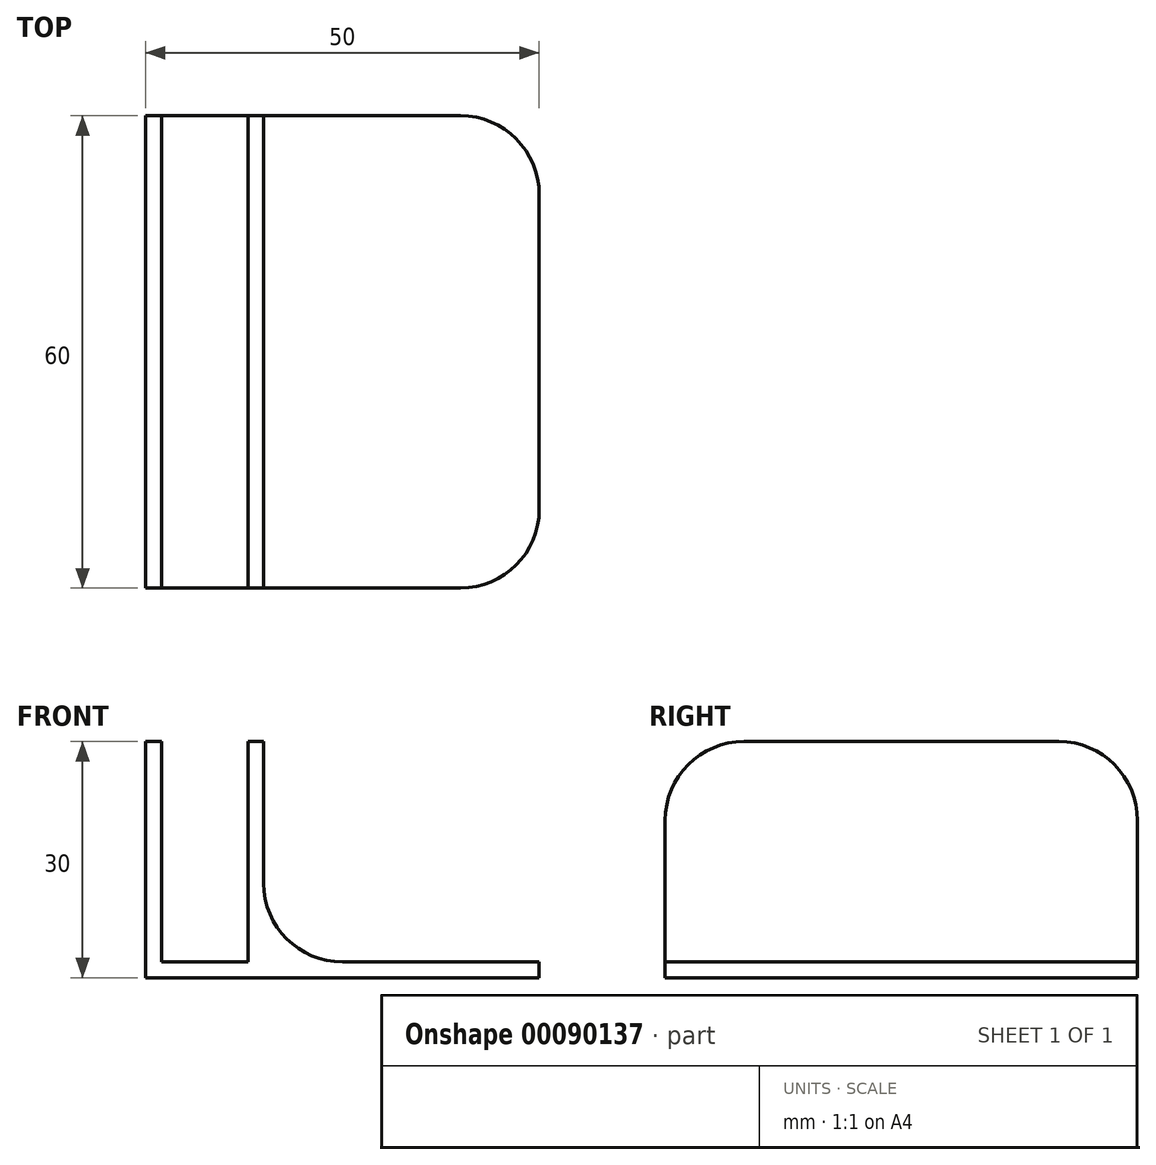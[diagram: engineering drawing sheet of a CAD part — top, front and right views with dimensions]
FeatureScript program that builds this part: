
annotation { "Feature Type Name" : "Feature", "Feature Type Description" : "" }
export const myFeature = defineFeature(function(context is Context, id is Id, definition is map)
    precondition{}
    {
        {
            var Q0;
            Q0=qCreatedBy(makeId("Front.planeOp"),FACE);
            var sketch = newSketch(context, id + "F0", { "sketchPlane" : qUnion([Q0])});
            skLineSegment(sketch, "E0.bottom", {"start": v(0, 0) * mm, "end": v(50, 0) * mm});
            skLineSegment(sketch, "E0.top", {"start": v(0, 2) * mm, "end": v(50, 2) * mm});
            skLineSegment(sketch, "E0.left", {"start": v(0, 0) * mm, "end": v(0, 2) * mm});
            skLineSegment(sketch, "E0.right", {"start": v(50, 0) * mm, "end": v(50, 2) * mm});
            skLineSegment(sketch, "E1.bottom", {"start": v(0, 0) * mm, "end": v(2, 0) * mm});
            skLineSegment(sketch, "E1.top", {"start": v(0, 30) * mm, "end": v(2, 30) * mm});
            skLineSegment(sketch, "E1.left", {"start": v(0, 0) * mm, "end": v(0, 30) * mm});
            skLineSegment(sketch, "E1.right", {"start": v(2, 0) * mm, "end": v(2, 30) * mm});
            skLineSegment(sketch, "E2.1.0.0", {"start": v(13, 0) * mm, "end": v(13, 30) * mm});
            skLineSegment(sketch, "E2.1.0.1", {"start": v(15, 0) * mm, "end": v(15, 30) * mm});
            skLineSegment(sketch, "E2.1.0.2", {"start": v(13, 0) * mm, "end": v(13, 2) * mm});
            skLineSegment(sketch, "E2.1.0.3", {"start": v(13, 0) * mm, "end": v(15, 0) * mm});
            skLineSegment(sketch, "E2.1.0.4", {"start": v(13, 30) * mm, "end": v(15, 30) * mm});
            skLineSegment(sketch, "E2.direction1", {"start": v(0, 0) * mm, "end": v(13, 0) * mm, "construction": true});
            skSolve(sketch);
        }
        {
            var Q0;
            Q0=qSketchRegion(id+"F0",true);
            extrude(context, id + "F1", {"entities" : qUnion([Q0]), "depth" : 60 * mm});
        }
        {
            var Q0;
            Q0=makeQuery(id+"F1.opExtrude","CAP_EDGE",EDGE,{"disambiguationData":[OSD([sQuery(id+"F0.wireOp",EDGE,"E2.1.0.4")])],"isStart":false});
            var Q1;
            Q1=makeQuery(id+"F1.opExtrude","CAP_EDGE",EDGE,{"disambiguationData":[OSD([sQuery(id+"F0.wireOp",EDGE,"E1.top")])],"isStart":false});
            var Q2;
            Q2=makeQuery(id+"F1.opExtrude","CAP_EDGE",EDGE,{"disambiguationData":[OSD([sQuery(id+"F0.wireOp",EDGE,"E2.1.0.4")])],"isStart":true});
            var Q3;
            Q3=makeQuery(id+"F1.opExtrude","CAP_EDGE",EDGE,{"disambiguationData":[OSD([sQuery(id+"F0.wireOp",EDGE,"E1.top")])],"isStart":true});
            var Q4;
            Q4=makeQuery(id+"F1.opExtrude","SWEPT_EDGE",EDGE,{"disambiguationData":[OSD([sQuery(id+"F0.wireOp",EDGE,"E0.top"),sQuery(id+"F0.wireOp",EDGE,"E2.1.0.1")])]});
            var Q5;
            Q5=makeQuery(id+"F1.opExtrude","CAP_EDGE",EDGE,{"disambiguationData":[OSD([sQuery(id+"F0.wireOp",EDGE,"E0.right")])],"isStart":true});
            var Q6;
            Q6=makeQuery(id+"F1.opExtrude","CAP_EDGE",EDGE,{"disambiguationData":[OSD([sQuery(id+"F0.wireOp",EDGE,"E0.right")])],"isStart":false});
            fillet(context, id + "F2", {"entities" : qUnion([Q0, Q1, Q2, Q3, Q4, Q5, Q6]), "radius" : 10 * mm, "tangentPropagation" : true, "allowEdgeOverflow" : false});
        }
    });
